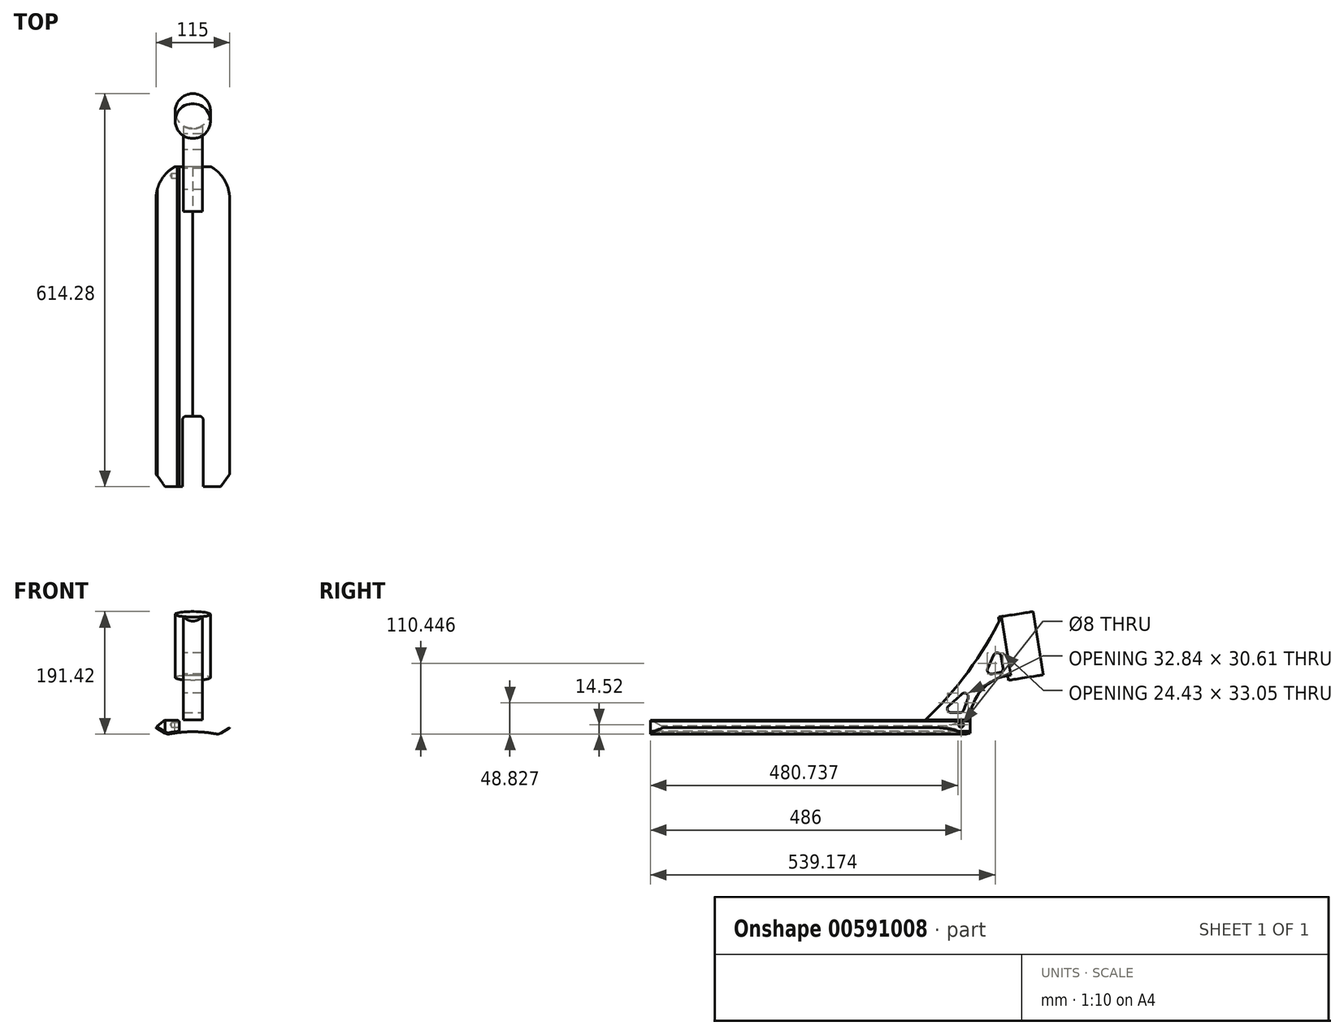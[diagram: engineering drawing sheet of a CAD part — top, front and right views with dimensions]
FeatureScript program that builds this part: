
annotation { "Feature Type Name" : "Feature", "Feature Type Description" : "" }
export const myFeature = defineFeature(function(context is Context, id is Id, definition is map)
    precondition{}
    {
        {
            var Q0;
            Q0=qCreatedBy(makeId("Front.planeOp"),FACE);
            var sketch = newSketch(context, id + "F0", { "sketchPlane" : qUnion([Q0])});
            skLineSegment(sketch, "E0", {"start": v(0, 21.26) * mm, "end": v(0, 0) * mm, "construction": true});
            skLineSegment(sketch, "E1", {"start": v(0, 18.1) * mm, "end": v(22.5, 18.1) * mm});
            skLineSegment(sketch, "E2", {"start": v(22.5, 18.1) * mm, "end": v(22.5, 19.4) * mm});
            skLineSegment(sketch, "E3", {"start": v(22.5, 19.4) * mm, "end": v(45.58, 19.4) * mm});
            skLineSegment(sketch, "E4", {"start": v(45.58, 19.4) * mm, "end": v(57.5, 9.4) * mm});
            skLineSegment(sketch, "E5", {"start": v(57.5, 9.4) * mm, "end": v(57.5, 5.4) * mm});
            skLineSegment(sketch, "E6", {"start": v(57.5, 5.4) * mm, "end": v(40.18, -4.6) * mm});
            skLineSegment(sketch, "E7.MirrorCS", {"start": v(0, 18.1) * mm, "end": v(-22.5, 18.1) * mm});
            skLineSegment(sketch, "E8.MirrorCS", {"start": v(-22.5, 19.4) * mm, "end": v(-45.58, 19.4) * mm});
            skLineSegment(sketch, "E9.MirrorCS", {"start": v(-45.58, 19.4) * mm, "end": v(-57.5, 9.4) * mm});
            skLineSegment(sketch, "E10.MirrorCS", {"start": v(-22.5, 18.1) * mm, "end": v(-22.5, 19.4) * mm});
            skLineSegment(sketch, "E11.MirrorCS", {"start": v(-57.5, 5.4) * mm, "end": v(-40.18, -4.6) * mm});
            skLineSegment(sketch, "E12.MirrorCS", {"start": v(-57.5, 9.4) * mm, "end": v(-57.5, 5.4) * mm});
            skArc(sketch, "E13", {"start": v(40.18, -4.6) * mm, "mid": v(0, -0.51) * mm, "end": v(-40.18, -4.6) * mm});
            skSolve(sketch);
        }
        {
            var Q0;
            Q0 = qSketchRegion(id + "F0", true);
            extrude(context, id + "F1", {"entities" : qUnion([Q0]), "endBound" : BoundingType.SYMMETRIC, "depth" : 500 * mm, "offsetDistance" : 25 * mm});
        }
        {
            var Q0;
            Q0=qCreatedBy(makeId("Front.planeOp"),FACE);
            var sketch = newSketch(context, id + "F2", { "sketchPlane" : qUnion([Q0])});
            skLineSegment(sketch, "E14", {"start": v(-19, 16.1) * mm, "end": v(19, 16.1) * mm});
            skLineSegment(sketch, "E15", {"start": v(19, 16.1) * mm, "end": v(19, 3.1) * mm});
            skLineSegment(sketch, "E16", {"start": v(19, 3.1) * mm, "end": v(-19, 3.1) * mm});
            skLineSegment(sketch, "E17", {"start": v(-19, 3.1) * mm, "end": v(-19, 16.1) * mm});
            skSolve(sketch);
        }
        {
            var Q0;
            Q0 = qSketchRegion(id + "F2", true);
            extrude(context, id + "F3", {"entities" : qUnion([Q0]), "operationType" : NewBodyOperationType.REMOVE, "endBound" : BoundingType.SYMMETRIC, "depth" : 500 * mm, "offsetDistance" : 25 * mm});
        }
        {
            var Q0;
            Q0=makeQuery(id+"F1.opExtrude","SWEPT_EDGE",EDGE,{"disambiguationData":[OSD([sQuery(id+"F0.wireOp",EDGE,"E8.MirrorCS"),sQuery(id+"F0.wireOp",EDGE,"E10.MirrorCS")])]});
            var Q1;
            Q1=makeQuery(id+"F1.opExtrude","SWEPT_EDGE",EDGE,{"disambiguationData":[OSD([sQuery(id+"F0.wireOp",EDGE,"E2"),sQuery(id+"F0.wireOp",EDGE,"E3")])]});
            fillet(context, id + "F4", {"entities" : qUnion([Q0, Q1]), "radius" : 2 * mm, "tangentPropagation" : true, "allowEdgeOverflow" : false});
        }
        {
            var Q0;
            Q0=makeQuery(id+"F1.opExtrude","SWEPT_EDGE",EDGE,{"disambiguationData":[OSD([sQuery(id+"F0.wireOp",EDGE,"E8.MirrorCS"),sQuery(id+"F0.wireOp",EDGE,"E9.MirrorCS")])]});
            var Q1;
            Q1=makeQuery(id+"F1.opExtrude","SWEPT_EDGE",EDGE,{"disambiguationData":[OSD([sQuery(id+"F0.wireOp",EDGE,"E3"),sQuery(id+"F0.wireOp",EDGE,"E4")])]});
            var Q2;
            Q2=makeQuery(id+"F1.opExtrude","SWEPT_EDGE",EDGE,{"disambiguationData":[OSD([sQuery(id+"F0.wireOp",EDGE,"E6"),sQuery(id+"F0.wireOp",EDGE,"E13")])]});
            var Q3;
            Q3=makeQuery(id+"F1.opExtrude","SWEPT_EDGE",EDGE,{"disambiguationData":[OSD([sQuery(id+"F0.wireOp",EDGE,"E11.MirrorCS"),sQuery(id+"F0.wireOp",EDGE,"E13")])]});
            fillet(context, id + "F5", {"entities" : qUnion([Q0, Q1, Q2, Q3]), "radius" : 9 * mm, "tangentPropagation" : true, "allowEdgeOverflow" : false});
        }
        {
            var Q0;
            Q0=makeQuery(id+"F1.opExtrude","SWEPT_EDGE",EDGE,{"disambiguationData":[OSD([sQuery(id+"F0.wireOp",EDGE,"E4"),sQuery(id+"F0.wireOp",EDGE,"E5")])]});
            var Q1;
            Q1=makeQuery(id+"F1.opExtrude","SWEPT_EDGE",EDGE,{"disambiguationData":[OSD([sQuery(id+"F0.wireOp",EDGE,"E5"),sQuery(id+"F0.wireOp",EDGE,"E6")])]});
            var Q2;
            Q2=makeQuery(id+"F1.opExtrude","SWEPT_EDGE",EDGE,{"disambiguationData":[OSD([sQuery(id+"F0.wireOp",EDGE,"E11.MirrorCS"),sQuery(id+"F0.wireOp",EDGE,"E12.MirrorCS")])]});
            var Q3;
            Q3=makeQuery(id+"F1.opExtrude","SWEPT_EDGE",EDGE,{"disambiguationData":[OSD([sQuery(id+"F0.wireOp",EDGE,"E9.MirrorCS"),sQuery(id+"F0.wireOp",EDGE,"E12.MirrorCS")])]});
            fillet(context, id + "F6", {"entities" : qUnion([Q0, Q1, Q2, Q3]), "radius" : 1 * mm, "tangentPropagation" : true, "allowEdgeOverflow" : false});
        }
        {
            var Q0;
            Q0=makeQuery(id+"F1.opExtrude","CAP_FACE",FACE,{"disambiguationData":[OSD([sQuery(id+"F0.wireOp",EDGE,"E1"),sQuery(id+"F0.wireOp",EDGE,"E2"),sQuery(id+"F0.wireOp",EDGE,"E3"),sQuery(id+"F0.wireOp",EDGE,"E4"),sQuery(id+"F0.wireOp",EDGE,"E5"),sQuery(id+"F0.wireOp",EDGE,"E6"),sQuery(id+"F0.wireOp",EDGE,"E7.MirrorCS"),sQuery(id+"F0.wireOp",EDGE,"E8.MirrorCS"),sQuery(id+"F0.wireOp",EDGE,"E9.MirrorCS"),sQuery(id+"F0.wireOp",EDGE,"E10.MirrorCS"),sQuery(id+"F0.wireOp",EDGE,"E11.MirrorCS"),sQuery(id+"F0.wireOp",EDGE,"E12.MirrorCS"),sQuery(id+"F0.wireOp",EDGE,"E13")])],"isStart":false});
            var sketch = newSketch(context, id + "F7", { "sketchPlane" : qUnion([Q0])});
            skLineSegment(sketch, "E18.0.0", {"start": v(-48.1, 17.3) * mm, "end": v(-57.14, 9.7) * mm});
            skArc(sketch, "E18.0.1", {"start": v(-57.14, 9.7) * mm, "mid": v(-57.4, 9.37) * mm, "end": v(-57.5, 8.94) * mm});
            skLineSegment(sketch, "E18.0.2", {"start": v(-57.5, 8.94) * mm, "end": v(-57.5, 5.99) * mm});
            skArc(sketch, "E18.0.3", {"start": v(-57.5, 5.99) * mm, "mid": v(-57.37, 5.49) * mm, "end": v(-57, 5.12) * mm});
            skLineSegment(sketch, "E18.0.4", {"start": v(-57, 5.12) * mm, "end": v(-43.1, -2.9) * mm});
            skArc(sketch, "E18.0.5", {"start": v(-43.1, -2.9) * mm, "mid": v(-40.12, -3.98) * mm, "end": v(-36.94, -3.95) * mm});
            skArc(sketch, "E18.0.6", {"start": v(-36.94, -3.95) * mm, "mid": v(0, -0.51) * mm, "end": v(36.94, -3.95) * mm});
            skArc(sketch, "E18.0.7", {"start": v(36.94, -3.95) * mm, "mid": v(40.12, -3.98) * mm, "end": v(43.1, -2.9) * mm});
            skLineSegment(sketch, "E18.0.8", {"start": v(43.1, -2.9) * mm, "end": v(57, 5.12) * mm});
            skArc(sketch, "E18.0.9", {"start": v(57, 5.12) * mm, "mid": v(57.37, 5.49) * mm, "end": v(57.5, 5.99) * mm});
            skLineSegment(sketch, "E18.0.10", {"start": v(57.5, 5.99) * mm, "end": v(57.5, 8.94) * mm});
            skArc(sketch, "E18.0.11", {"start": v(57.5, 8.94) * mm, "mid": v(57.4, 9.37) * mm, "end": v(57.14, 9.7) * mm});
            skLineSegment(sketch, "E18.0.12", {"start": v(57.14, 9.7) * mm, "end": v(48.1, 17.3) * mm});
            skArc(sketch, "E18.0.13", {"start": v(48.1, 17.3) * mm, "mid": v(45.38, 18.87) * mm, "end": v(42.3, 19.4) * mm});
            skLineSegment(sketch, "E18.0.14", {"start": v(42.3, 19.4) * mm, "end": v(24.37, 19.4) * mm});
            skArc(sketch, "E18.0.15", {"start": v(24.37, 19.4) * mm, "mid": v(23.23, 19.05) * mm, "end": v(22.5, 18.1) * mm});
            skLineSegment(sketch, "E18.0.16", {"start": v(22.5, 18.1) * mm, "end": v(-22.5, 18.1) * mm});
            skArc(sketch, "E18.0.17", {"start": v(-22.5, 18.1) * mm, "mid": v(-23.23, 19.05) * mm, "end": v(-24.37, 19.4) * mm});
            skLineSegment(sketch, "E18.0.18", {"start": v(-24.37, 19.4) * mm, "end": v(-42.3, 19.4) * mm});
            skArc(sketch, "E18.0.19", {"start": v(-42.3, 19.4) * mm, "mid": v(-45.38, 18.87) * mm, "end": v(-48.1, 17.3) * mm});
            skArc(sketch, "E19.0", {"start": v(-37.3, -1.99) * mm, "mid": v(-29.18, -0.63) * mm, "end": v(-21, 0.4) * mm});
            skArc(sketch, "E19.1", {"start": v(-42.1, -1.17) * mm, "mid": v(-39.78, -2) * mm, "end": v(-37.3, -1.99) * mm});
            skLineSegment(sketch, "E19.2", {"start": v(-24.37, 17.4) * mm, "end": v(-42.3, 17.4) * mm});
            skArc(sketch, "E19.3", {"start": v(-42.3, 17.4) * mm, "mid": v(-44.7, 16.99) * mm, "end": v(-46.8, 15.77) * mm});
            skLineSegment(sketch, "E19.4", {"start": v(-46.8, 15.77) * mm, "end": v(-55.76, 8.26) * mm});
            skLineSegment(sketch, "E19.5", {"start": v(-55.61, 6.63) * mm, "end": v(-42.1, -1.17) * mm});
            skLineSegment(sketch, "E20.0", {"start": v(-21, 16.1) * mm, "end": v(-22.5, 16.1) * mm});
            skLineSegment(sketch, "E21.0", {"start": v(-21, 3.1) * mm, "end": v(-21, 16.1) * mm});
            skLineSegment(sketch, "E22", {"start": v(-21, 0.4) * mm, "end": v(-21, 3.1) * mm});
            skArc(sketch, "E23", {"start": v(-22.5, 16.1) * mm, "mid": v(-23.23, 17.05) * mm, "end": v(-24.37, 17.4) * mm});
            skPoint(sketch, "E24.visualSharp", {"position": v(-56.85, 7.34) * mm});
            skArc(sketch, "E24.filletArc", {"start": v(-55.76, 8.26) * mm, "mid": v(-56.1, 7.4) * mm, "end": v(-55.61, 6.63) * mm});
            skLineSegment(sketch, "E25", {"start": v(0, 29.26) * mm, "end": v(0, -8.55) * mm, "construction": true});
            skLineSegment(sketch, "E26.MirrorCS", {"start": v(21, 3.1) * mm, "end": v(21, 16.1) * mm});
            skLineSegment(sketch, "E27.MirrorCS", {"start": v(21, 16.1) * mm, "end": v(22.5, 16.1) * mm});
            skArc(sketch, "E28.MirrorCS", {"start": v(22.5, 16.1) * mm, "mid": v(23.23, 17.05) * mm, "end": v(24.37, 17.4) * mm});
            skLineSegment(sketch, "E29.MirrorCS", {"start": v(21, 0.4) * mm, "end": v(21, 3.1) * mm});
            skArc(sketch, "E30.MirrorCS", {"start": v(37.3, -1.99) * mm, "mid": v(29.18, -0.63) * mm, "end": v(21, 0.4) * mm});
            skLineSegment(sketch, "E31.MirrorCS", {"start": v(24.37, 17.4) * mm, "end": v(42.3, 17.4) * mm});
            skArc(sketch, "E32.MirrorCS", {"start": v(42.3, 17.4) * mm, "mid": v(44.7, 16.99) * mm, "end": v(46.8, 15.77) * mm});
            skLineSegment(sketch, "E33.MirrorCS", {"start": v(46.8, 15.77) * mm, "end": v(55.76, 8.26) * mm});
            skArc(sketch, "E34.MirrorCS", {"start": v(55.76, 8.26) * mm, "mid": v(56.1, 7.4) * mm, "end": v(55.61, 6.63) * mm});
            skLineSegment(sketch, "E35.MirrorCS", {"start": v(55.61, 6.63) * mm, "end": v(42.1, -1.17) * mm});
            skArc(sketch, "E36.MirrorCS", {"start": v(42.1, -1.17) * mm, "mid": v(39.78, -2) * mm, "end": v(37.3, -1.99) * mm});
            skSolve(sketch);
        }
        {
            var Q0;
            Q0=makeQuery(id+"F7.imprint","IMPRINT",FACE,{"disambiguationData":[TD([[makeQuery(id+"F7.imprint","IMPRINT",EDGE,{"derivedFrom":sQuery(id+"F7.wireOp",EDGE,"E26.MirrorCS")}),-1.0]])]});
            var Q1;
            Q1=makeQuery(id+"F7.imprint","IMPRINT",FACE,{"disambiguationData":[TD([[makeQuery(id+"F7.imprint","IMPRINT",EDGE,{"derivedFrom":sQuery(id+"F7.wireOp",EDGE,"E19.0")}),1.0]])]});
            extrude(context, id + "F8", {"entities" : qUnion([Q0, Q1]), "operationType" : NewBodyOperationType.REMOVE, "endBound" : BoundingType.THROUGH_ALL, "oppositeDirection" : true, "depth" : 25 * mm, "offsetDistance" : 25 * mm});
        }
        {
            var Q0;
            Q0=qCreatedBy(makeId("Top.planeOp"),FACE);
            var sketch = newSketch(context, id + "F9", { "sketchPlane" : qUnion([Q0])});
            skArc(sketch, "E37", {"start": v(57.5, 200) * mm, "mid": v(0, 257.5) * mm, "end": v(-57.5, 200) * mm});
            skLineSegment(sketch, "E38", {"start": v(-57.5, 280) * mm, "end": v(57.5, 280) * mm});
            skLineSegment(sketch, "E39", {"start": v(57.5, 280) * mm, "end": v(57.5, 200) * mm});
            skLineSegment(sketch, "E40", {"start": v(-57.5, 280) * mm, "end": v(-57.5, 200) * mm});
            skSolve(sketch);
        }
        {
            var Q0;
            Q0 = qSketchRegion(id + "F9", true);
            extrude(context, id + "F10", {"entities" : qUnion([Q0]), "operationType" : NewBodyOperationType.REMOVE, "endBound" : BoundingType.THROUGH_ALL, "oppositeDirection" : true, "depth" : 25 * mm, "offsetDistance" : 25 * mm, "hasSecondDirection" : true, "secondDirectionBound" : SecondDirectionBoundingType.THROUGH_ALL, "secondDirectionOppositeDirection" : false, "secondDirectionDepth" : 25 * mm});
        }
        {
            var Q0;
            Q0=qCreatedBy(makeId("Top.planeOp"),FACE);
            var sketch = newSketch(context, id + "F11", { "sketchPlane" : qUnion([Q0])});
            skLineSegment(sketch, "E41", {"start": v(-68, -216) * mm, "end": v(-68, -346) * mm});
            skLineSegment(sketch, "E42", {"start": v(-68, -346) * mm, "end": v(68, -346) * mm});
            skLineSegment(sketch, "E43", {"start": v(68, -346) * mm, "end": v(68, -216) * mm});
            skLineSegment(sketch, "E44", {"start": v(68, -216) * mm, "end": v(43.3, -250) * mm});
            skLineSegment(sketch, "E45", {"start": v(43.3, -250) * mm, "end": v(16, -250) * mm});
            skLineSegment(sketch, "E46", {"start": v(16, -250) * mm, "end": v(16, -140) * mm});
            skLineSegment(sketch, "E47", {"start": v(16, -140) * mm, "end": v(-16, -140) * mm});
            skLineSegment(sketch, "E48", {"start": v(-16, -140) * mm, "end": v(-16, -250) * mm});
            skLineSegment(sketch, "E49", {"start": v(-16, -250) * mm, "end": v(-43.3, -250) * mm});
            skLineSegment(sketch, "E50", {"start": v(-43.3, -250) * mm, "end": v(-68, -216) * mm});
            skSolve(sketch);
        }
        {
            var Q0;
            Q0 = qSketchRegion(id + "F11", true);
            extrude(context, id + "F12", {"entities" : qUnion([Q0]), "operationType" : NewBodyOperationType.REMOVE, "endBound" : BoundingType.THROUGH_ALL, "depth" : 25 * mm, "offsetDistance" : 25 * mm, "hasSecondDirection" : true, "secondDirectionBound" : SecondDirectionBoundingType.THROUGH_ALL, "secondDirectionOppositeDirection" : true, "secondDirectionDepth" : 25 * mm});
        }
        {
            var Q0;
            {var subQ0=sQuery(id+"F11.wireOp",EDGE,"E47");var subQ1=sQuery(id+"F11.wireOp",EDGE,"E48");Q0=makeQuery(id+"F12.boolean.opBoolean","COPY",EDGE,{"disambiguationData":[TD([makeQuery(id+"F3.boolean.opBoolean","COPY",FACE,{"derivedFrom":makeQuery(id+"F3.opExtrude","SWEPT_FACE",FACE,{"disambiguationData":[OSD([sQuery(id+"F2.wireOp",EDGE,"E14")])]})})])],"derivedFrom":makeQuery(id+"F12.opExtrude","SWEPT_EDGE",EDGE,{"disambiguationData":[OSD([subQ0,subQ1])]})});}
            var Q1;
            {var subQ0=sQuery(id+"F11.wireOp",EDGE,"E48");var subQ1=sQuery(id+"F11.wireOp",EDGE,"E47");Q1=makeQuery(id+"F12.boolean.opBoolean","COPY",EDGE,{"disambiguationData":[TD([makeQuery(id+"F1.opExtrude","SWEPT_FACE",FACE,{"disambiguationData":[OSD([sQuery(id+"F0.wireOp",EDGE,"E13")])]})])],"derivedFrom":makeQuery(id+"F12.opExtrude","SWEPT_EDGE",EDGE,{"disambiguationData":[OSD([subQ1,subQ0])]})});}
            var Q2;
            {var subQ2=sQuery(id+"F11.wireOp",EDGE,"E48");Q2=makeQuery(id+"F12.boolean.opBoolean","COPY",EDGE,{"disambiguationData":[TD([makeQuery(id+"F3.boolean.opBoolean","COPY",FACE,{"derivedFrom":makeQuery(id+"F3.opExtrude","SWEPT_FACE",FACE,{"disambiguationData":[OSD([sQuery(id+"F2.wireOp",EDGE,"E14")])]})})])],"derivedFrom":makeQuery(id+"F12.opExtrude","SWEPT_EDGE",EDGE,{"disambiguationData":[OSD([subQ2,sQuery(id+"F11.wireOp",EDGE,"E49")])]})});}
            var Q3;
            {var subQ0=sQuery(id+"F11.wireOp",EDGE,"E47");var subQ1=sQuery(id+"F11.wireOp",EDGE,"E46");Q3=makeQuery(id+"F12.boolean.opBoolean","COPY",EDGE,{"disambiguationData":[TD([makeQuery(id+"F3.boolean.opBoolean","COPY",FACE,{"derivedFrom":makeQuery(id+"F3.opExtrude","SWEPT_FACE",FACE,{"disambiguationData":[OSD([sQuery(id+"F2.wireOp",EDGE,"E14")])]})})])],"derivedFrom":makeQuery(id+"F12.opExtrude","SWEPT_EDGE",EDGE,{"disambiguationData":[OSD([subQ1,subQ0])]})});}
            var Q4;
            {var subQ0=sQuery(id+"F11.wireOp",EDGE,"E46");var subQ1=sQuery(id+"F11.wireOp",EDGE,"E47");Q4=makeQuery(id+"F12.boolean.opBoolean","COPY",EDGE,{"disambiguationData":[TD([makeQuery(id+"F1.opExtrude","SWEPT_FACE",FACE,{"disambiguationData":[OSD([sQuery(id+"F0.wireOp",EDGE,"E13")])]})])],"derivedFrom":makeQuery(id+"F12.opExtrude","SWEPT_EDGE",EDGE,{"disambiguationData":[OSD([subQ0,subQ1])]})});}
            var Q5;
            {var subQ2=sQuery(id+"F11.wireOp",EDGE,"E46");Q5=makeQuery(id+"F12.boolean.opBoolean","COPY",EDGE,{"disambiguationData":[TD([makeQuery(id+"F3.boolean.opBoolean","COPY",FACE,{"derivedFrom":makeQuery(id+"F3.opExtrude","SWEPT_FACE",FACE,{"disambiguationData":[OSD([sQuery(id+"F2.wireOp",EDGE,"E14")])]})})])],"derivedFrom":makeQuery(id+"F12.opExtrude","SWEPT_EDGE",EDGE,{"disambiguationData":[OSD([sQuery(id+"F11.wireOp",EDGE,"E45"),subQ2])]})});}
            var Q6;
            {var subQ0=sQuery(id+"F0.wireOp",EDGE,"E13");var subQ1=sQuery(id+"F11.wireOp",EDGE,"E48");Q6=makeQuery(id+"F12.boolean.opBoolean","COPY",EDGE,{"disambiguationData":[TD([makeQuery(id+"F1.opExtrude","SWEPT_FACE",FACE,{"disambiguationData":[OSD([subQ0])]})])],"derivedFrom":makeQuery(id+"F12.opExtrude","SWEPT_EDGE",EDGE,{"disambiguationData":[OSD([subQ1,sQuery(id+"F11.wireOp",EDGE,"E49")])]})});}
            var Q7;
            {var subQ0=sQuery(id+"F0.wireOp",EDGE,"E13");var subQ1=sQuery(id+"F11.wireOp",EDGE,"E46");Q7=makeQuery(id+"F12.boolean.opBoolean","COPY",EDGE,{"disambiguationData":[TD([makeQuery(id+"F1.opExtrude","SWEPT_FACE",FACE,{"disambiguationData":[OSD([subQ0])]})])],"derivedFrom":makeQuery(id+"F12.opExtrude","SWEPT_EDGE",EDGE,{"disambiguationData":[OSD([sQuery(id+"F11.wireOp",EDGE,"E45"),subQ1])]})});}
            fillet(context, id + "F13", {"entities" : qUnion([Q0, Q1, Q2, Q3, Q4, Q5, Q6, Q7]), "radius" : 5 * mm, "tangentPropagation" : true, "allowEdgeOverflow" : false});
        }
        {
            var Q0;
            Q0=makeQuery(id+"F8.boolean.opBoolean","COPY",FACE,{"derivedFrom":makeQuery(id+"F8.opExtrude","SWEPT_FACE",FACE,{"disambiguationData":[OSD([sQuery(id+"F7.wireOp",EDGE,"E26.MirrorCS"),sQuery(id+"F7.wireOp",EDGE,"E29.MirrorCS")])]})});
            var sketch = newSketch(context, id + "F14", { "sketchPlane" : qUnion([Q0])});
            skPoint(sketch, "E51", {"position": v(-236, 10.4) * mm});
            skSolve(sketch);
        }
        {
            var Q0;
            Q0=makeQuery(id+"F8.boolean.opBoolean","COPY",FACE,{"derivedFrom":makeQuery(id+"F8.opExtrude","SWEPT_FACE",FACE,{"disambiguationData":[OSD([sQuery(id+"F7.wireOp",EDGE,"E21.0"),sQuery(id+"F7.wireOp",EDGE,"E22")])]})});
            var sketch = newSketch(context, id + "F15", { "sketchPlane" : qUnion([Q0])});
            skPoint(sketch, "E52", {"position": v(236, 10.4) * mm});
            skSolve(sketch);
        }
        {
            var Q0;
            Q0=sQuery(id+"F14.wireOp",VERTEX,"E51");
            var Q1;
            Q1=sQuery(id+"F15.wireOp",VERTEX,"E52");
            var Q2;
            Q2=makeQuery(id+"F1.opExtrude","SWEPT_BODY",BODY,{"disambiguationData":[OSD([sQuery(id+"F0.wireOp",EDGE,"E1"),sQuery(id+"F0.wireOp",EDGE,"E2"),sQuery(id+"F0.wireOp",EDGE,"E3"),sQuery(id+"F0.wireOp",EDGE,"E4"),sQuery(id+"F0.wireOp",EDGE,"E5"),sQuery(id+"F0.wireOp",EDGE,"E6"),sQuery(id+"F0.wireOp",EDGE,"E7.MirrorCS"),sQuery(id+"F0.wireOp",EDGE,"E8.MirrorCS"),sQuery(id+"F0.wireOp",EDGE,"E9.MirrorCS"),sQuery(id+"F0.wireOp",EDGE,"E10.MirrorCS"),sQuery(id+"F0.wireOp",EDGE,"E11.MirrorCS"),sQuery(id+"F0.wireOp",EDGE,"E12.MirrorCS"),sQuery(id+"F0.wireOp",EDGE,"E13")])]});
            hole(context, id + "F16", {"style" : HoleStyle.SIMPLE, "endStyle" : HoleEndStyle.BLIND, "holeDiameter" : 8 * mm, "majorDiameter" : 5 * mm, "holeDepth" : 12 * mm, "isTappedThrough" : true, "tappedDepth" : 12 * mm, "tapClearance" : 3, "locations" : qUnion([Q0, Q1]), "scope" : qUnion([Q2])});
        }
        {
            var Q0;
            Q0=qCreatedBy(makeId("Right.planeOp"),FACE);
            var sketch = newSketch(context, id + "F17", { "sketchPlane" : qUnion([Q0])});
            skLineSegment(sketch, "E53", {"start": v(180, 18.1) * mm, "end": v(250, 18.1) * mm});
            skLineSegment(sketch, "E54", {"start": v(298.76, 179.4) * mm, "end": v(344.2, 186.6) * mm});
            skLineSegment(sketch, "E55", {"start": v(344.2, 186.6) * mm, "end": v(359.84, 87.84) * mm});
            skLineSegment(sketch, "E56", {"start": v(359.84, 87.84) * mm, "end": v(314.4, 80.64) * mm});
            skLineSegment(sketch, "E57", {"start": v(314.4, 80.64) * mm, "end": v(313.28, 87.79) * mm});
            skArc(sketch, "E58", {"start": v(180, 18.1) * mm, "mid": v(246.79, 93.3) * mm, "end": v(298.76, 179.4) * mm});
            skArc(sketch, "E59", {"start": v(313.28, 87.79) * mm, "mid": v(268.18, 65.17) * mm, "end": v(250, 18.1) * mm});
            skSolve(sketch);
        }
        {
            var Q0;
            Q0 = qSketchRegion(id + "F17", true);
            extrude(context, id + "F18", {"entities" : qUnion([Q0]), "operationType" : NewBodyOperationType.ADD, "endBound" : BoundingType.SYMMETRIC, "depth" : 30 * mm, "offsetDistance" : 25 * mm});
        }
        {
            var Q0;
            Q0=makeQuery(id+"F18.opExtrude","SWEPT_FACE",FACE,{"disambiguationData":[OSD([sQuery(id+"F17.wireOp",EDGE,"E54")])]});
            var sketch = newSketch(context, id + "F19", { "sketchPlane" : qUnion([Q0])});
            skCircle(sketch, "E60", {"center": v(0, 346.15) * mm, "radius": 27.5 * mm});
            skSolve(sketch);
        }
        {
            var Q0;
            Q0 = qSketchRegion(id + "F19", true);
            var Q1;
            Q1=makeQuery(id+"F18.opExtrude","SWEPT_FACE",FACE,{"disambiguationData":[OSD([sQuery(id+"F17.wireOp",EDGE,"E56")])]});
            extrude(context, id + "F20", {"entities" : qUnion([Q0]), "operationType" : NewBodyOperationType.ADD, "endBound" : BoundingType.UP_TO_SURFACE, "oppositeDirection" : true, "depth" : 25 * mm, "endBoundEntityFace" : qUnion([Q1]), "offsetDistance" : 25 * mm});
        }
        {
            var Q0;
            Q0=makeQuery(id+"F20.boolean.opBoolean","MERGE",FACE,{"derivedFrom":[makeQuery(id+"F18.opExtrude","SWEPT_FACE",FACE,{"disambiguationData":[OSD([sQuery(id+"F17.wireOp",EDGE,"E54")])]}),makeQuery(id+"F20.opExtrude","CAP_FACE",FACE,{"disambiguationData":[OSD([sQuery(id+"F19.wireOp",EDGE,"E60")])],"isStart":true})]});
            var sketch = newSketch(context, id + "F21", { "sketchPlane" : qUnion([Q0])});
            skPoint(sketch, "E61", {"position": v(0, 346.15) * mm});
            skSolve(sketch);
        }
        {
            var Q0;
            Q0=sQuery(id+"F21.wireOp",VERTEX,"E61");
            var Q1;
            Q1=makeQuery(id+"F1.opExtrude","SWEPT_BODY",BODY,{"disambiguationData":[OSD([sQuery(id+"F0.wireOp",EDGE,"E1"),sQuery(id+"F0.wireOp",EDGE,"E2"),sQuery(id+"F0.wireOp",EDGE,"E3"),sQuery(id+"F0.wireOp",EDGE,"E4"),sQuery(id+"F0.wireOp",EDGE,"E5"),sQuery(id+"F0.wireOp",EDGE,"E6"),sQuery(id+"F0.wireOp",EDGE,"E7.MirrorCS"),sQuery(id+"F0.wireOp",EDGE,"E8.MirrorCS"),sQuery(id+"F0.wireOp",EDGE,"E9.MirrorCS"),sQuery(id+"F0.wireOp",EDGE,"E10.MirrorCS"),sQuery(id+"F0.wireOp",EDGE,"E11.MirrorCS"),sQuery(id+"F0.wireOp",EDGE,"E12.MirrorCS"),sQuery(id+"F0.wireOp",EDGE,"E13")])]});
            hole(context, id + "F22", {"style" : HoleStyle.SIMPLE, "endStyle" : HoleEndStyle.THROUGH, "holeDiameter" : 40 * mm, "majorDiameter" : 5 * mm, "isTappedThrough" : true, "tappedDepth" : 12 * mm, "tapClearance" : 3, "locations" : qUnion([Q0]), "scope" : qUnion([Q1])});
        }
        {
            var Q0;
            Q0=makeQuery(id+"F18.opExtrude","CAP_FACE",FACE,{"disambiguationData":[OSD([sQuery(id+"F17.wireOp",EDGE,"E53"),sQuery(id+"F17.wireOp",EDGE,"E54"),sQuery(id+"F17.wireOp",EDGE,"E55"),sQuery(id+"F17.wireOp",EDGE,"E56"),sQuery(id+"F17.wireOp",EDGE,"E57"),sQuery(id+"F17.wireOp",EDGE,"E58"),sQuery(id+"F17.wireOp",EDGE,"E59")])],"isStart":false});
            var sketch = newSketch(context, id + "F23", { "sketchPlane" : qUnion([Q0])});
            skLineSegment(sketch, "E62", {"start": v(204.58, 29.4) * mm, "end": v(238.58, 29.4) * mm});
            skLineSegment(sketch, "E63", {"start": v(238.58, 29.4) * mm, "end": v(254.96, 74.4) * mm});
            skLineSegment(sketch, "E64", {"start": v(254.96, 74.4) * mm, "end": v(204.58, 29.4) * mm});
            skLineSegment(sketch, "E65", {"start": v(295.2, 137.72) * mm, "end": v(302.23, 93.27) * mm});
            skPoint(sketch, "E65.endSnap0", {"position": v(246.76, 93.27) * mm});
            skLineSegment(sketch, "E66", {"start": v(302.23, 93.27) * mm, "end": v(272.74, 87.78) * mm});
            skLineSegment(sketch, "E67", {"start": v(272.74, 87.78) * mm, "end": v(295.2, 137.72) * mm});
            skSolve(sketch);
        }
        {
            var Q0;
            Q0 = qSketchRegion(id + "F23", true);
            extrude(context, id + "F24", {"entities" : qUnion([Q0]), "operationType" : NewBodyOperationType.REMOVE, "endBound" : BoundingType.THROUGH_ALL, "oppositeDirection" : true, "depth" : 25 * mm, "offsetDistance" : 25 * mm});
        }
        {
            var Q0;
            Q0=makeQuery(id+"F24.boolean.opBoolean","COPY",EDGE,{"derivedFrom":makeQuery(id+"F24.opExtrude","SWEPT_EDGE",EDGE,{"disambiguationData":[OSD([sQuery(id+"F23.wireOp",EDGE,"E65"),sQuery(id+"F23.wireOp",EDGE,"E67")])]})});
            var Q1;
            Q1=makeQuery(id+"F24.boolean.opBoolean","COPY",EDGE,{"derivedFrom":makeQuery(id+"F24.opExtrude","SWEPT_EDGE",EDGE,{"disambiguationData":[OSD([sQuery(id+"F23.wireOp",EDGE,"E66"),sQuery(id+"F23.wireOp",EDGE,"E67")])]})});
            var Q2;
            Q2=makeQuery(id+"F24.boolean.opBoolean","COPY",EDGE,{"derivedFrom":makeQuery(id+"F24.opExtrude","SWEPT_EDGE",EDGE,{"disambiguationData":[OSD([sQuery(id+"F23.wireOp",EDGE,"E65"),sQuery(id+"F23.wireOp",EDGE,"E66")])]})});
            var Q3;
            Q3=makeQuery(id+"F24.boolean.opBoolean","COPY",EDGE,{"derivedFrom":makeQuery(id+"F24.opExtrude","SWEPT_EDGE",EDGE,{"disambiguationData":[OSD([sQuery(id+"F23.wireOp",EDGE,"E63"),sQuery(id+"F23.wireOp",EDGE,"E64")])]})});
            var Q4;
            Q4=makeQuery(id+"F24.boolean.opBoolean","COPY",EDGE,{"derivedFrom":makeQuery(id+"F24.opExtrude","SWEPT_EDGE",EDGE,{"disambiguationData":[OSD([sQuery(id+"F23.wireOp",EDGE,"E62"),sQuery(id+"F23.wireOp",EDGE,"E64")])]})});
            var Q5;
            Q5=makeQuery(id+"F24.boolean.opBoolean","COPY",EDGE,{"derivedFrom":makeQuery(id+"F24.opExtrude","SWEPT_EDGE",EDGE,{"disambiguationData":[OSD([sQuery(id+"F23.wireOp",EDGE,"E62"),sQuery(id+"F23.wireOp",EDGE,"E63")])]})});
            fillet(context, id + "F25", {"entities" : qUnion([Q0, Q1, Q2, Q3, Q4, Q5]), "radius" : 6 * mm, "tangentPropagation" : true, "allowEdgeOverflow" : false});
        }
    });
